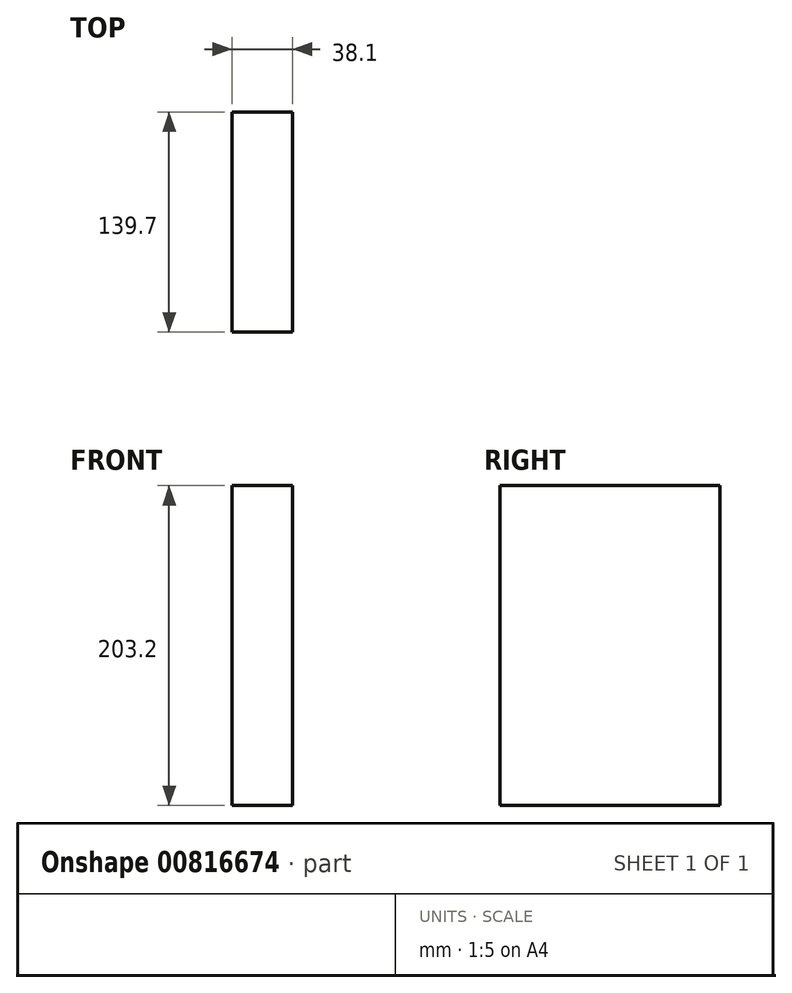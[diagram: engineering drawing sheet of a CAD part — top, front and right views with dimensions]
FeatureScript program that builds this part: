
annotation { "Feature Type Name" : "Feature", "Feature Type Description" : "" }
export const myFeature = defineFeature(function(context is Context, id is Id, definition is map)
    precondition{}
    {
        {
            var Q0;
            Q0=qCreatedBy(makeId("Right.planeOp"),FACE);
            var sketch = newSketch(context, id + "F0", { "sketchPlane" : qUnion([Q0])});
            skLineSegment(sketch, "E0.bottom", {"start": v(-83.22, -543.65) * mm, "end": v(56.48, -543.65) * mm});
            skLineSegment(sketch, "E0.top", {"start": v(-83.22, -746.85) * mm, "end": v(56.48, -746.85) * mm});
            skLineSegment(sketch, "E0.left", {"start": v(-83.22, -543.65) * mm, "end": v(-83.22, -746.85) * mm});
            skLineSegment(sketch, "E0.right", {"start": v(56.48, -543.65) * mm, "end": v(56.48, -746.85) * mm});
            skSolve(sketch);
        }
        {
            var Q0;
            Q0 = qSketchRegion(id + "F0", true);
            extrude(context, id + "F1", {"entities" : qUnion([Q0]), "depth" : 38.1 * mm, "offsetDistance" : 25.4 * mm});
        }
    });
